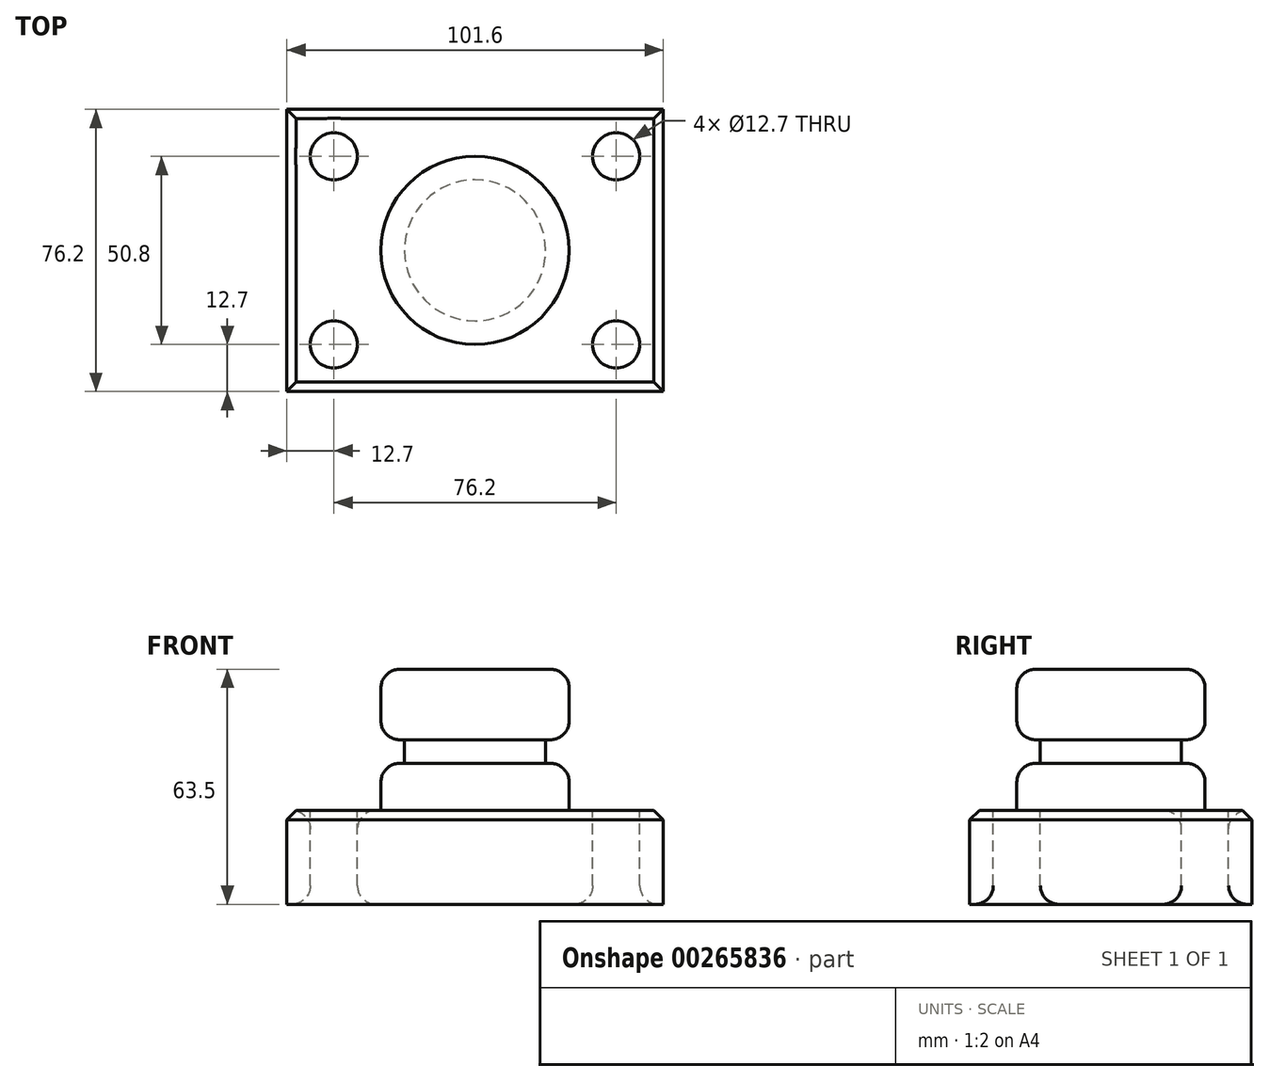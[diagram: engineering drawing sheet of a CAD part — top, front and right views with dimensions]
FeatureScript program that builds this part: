
annotation { "Feature Type Name" : "Feature", "Feature Type Description" : "" }
export const myFeature = defineFeature(function(context is Context, id is Id, definition is map)
    precondition{}
    {
        {
            var Q0;
            Q0=qCreatedBy(makeId("Top.planeOp"),FACE);
            var sketch = newSketch(context, id + "F0", { "sketchPlane" : qUnion([Q0])});
            skLineSegment(sketch, "E0.bottom", {"start": v(-50.8, 38.1) * mm, "end": v(50.8, 38.1) * mm});
            skLineSegment(sketch, "E0.top", {"start": v(-50.8, -38.1) * mm, "end": v(50.8, -38.1) * mm});
            skLineSegment(sketch, "E0.left", {"start": v(-50.8, 38.1) * mm, "end": v(-50.8, -38.1) * mm});
            skLineSegment(sketch, "E0.right", {"start": v(50.8, 38.1) * mm, "end": v(50.8, -38.1) * mm});
            skPoint(sketch, "E0.middle", {"position": v(0, 0) * mm});
            skSolve(sketch);
        }
        {
            var Q0;
            Q0 = qSketchRegion(id + "F0", true);
            extrude(context, id + "F1", {"entities" : qUnion([Q0]), "depth" : 25.4 * mm});
        }
        {
            var Q0;
            Q0=qCreatedBy(makeId("Top.planeOp"),FACE);
            var sketch = newSketch(context, id + "F2", { "sketchPlane" : qUnion([Q0])});
            skCircle(sketch, "E1", {"center": v(-38.1, 25.4) * mm, "radius": 6.35 * mm});
            skCircle(sketch, "E2", {"center": v(38.1, 25.4) * mm, "radius": 6.35 * mm});
            skCircle(sketch, "E3", {"center": v(-38.1, -25.4) * mm, "radius": 6.35 * mm});
            skCircle(sketch, "E4", {"center": v(38.1, -25.4) * mm, "radius": 6.35 * mm});
            skSolve(sketch);
        }
        {
            var Q0;
            Q0 = qSketchRegion(id + "F2", true);
            extrude(context, id + "F3", {"entities" : qUnion([Q0]), "operationType" : NewBodyOperationType.REMOVE, "oppositeDirection" : true, "depth" : 25.4 * mm, "hasSecondDirection" : true, "secondDirectionOppositeDirection" : false, "secondDirectionDepth" : 25.4 * mm});
        }
        {
            var Q0;
            Q0=qCreatedBy(makeId("Front.planeOp"),FACE);
            var sketch = newSketch(context, id + "F4", { "sketchPlane" : qUnion([Q0])});
            skLineSegment(sketch, "E5.bottom", {"start": v(0, 63.5) * mm, "end": v(25.4, 63.5) * mm});
            skLineSegment(sketch, "E5.top", {"start": v(0, 25.4) * mm, "end": v(25.4, 25.4) * mm});
            skLineSegment(sketch, "E5.left", {"start": v(0, 63.5) * mm, "end": v(0, 25.4) * mm});
            skLineSegment(sketch, "E5.right", {"start": v(25.4, 63.5) * mm, "end": v(25.4, 25.4) * mm});
            skSolve(sketch);
        }
        {
            var Q0;
            Q0 = qSketchRegion(id + "F4", true);
            var Q1;
            Q1=sQuery(id+"F4.wireOp",EDGE,"E5.left");
            revolve(context, id + "F5", {"operationType" : NewBodyOperationType.ADD, "entities" : qUnion([Q0]), "axis" : qUnion([Q1]), "revolveType" : RevolveType.FULL});
        }
        {
            var Q0;
            Q0=qCreatedBy(makeId("Right.planeOp"),FACE);
            var sketch = newSketch(context, id + "F6", { "sketchPlane" : qUnion([Q0])});
            skLineSegment(sketch, "E6.bottom", {"start": v(-38.1, 44.45) * mm, "end": v(-19.05, 44.45) * mm});
            skLineSegment(sketch, "E6.top", {"start": v(-38.1, 38.1) * mm, "end": v(-19.05, 38.1) * mm});
            skLineSegment(sketch, "E6.left", {"start": v(-38.1, 44.45) * mm, "end": v(-38.1, 38.1) * mm});
            skLineSegment(sketch, "E6.right", {"start": v(-19.05, 44.45) * mm, "end": v(-19.05, 38.1) * mm});
            skSolve(sketch);
        }
        {
            var Q0;
            Q0 = qSketchRegion(id + "F6", true);
            var Q1;
            Q1=makeQuery(id+"F5.opRevolve","SWEPT_FACE",FACE,{"disambiguationData":[OSD([sQuery(id+"F4.wireOp",EDGE,"E5.right")])]});
            revolve(context, id + "F7", {"operationType" : NewBodyOperationType.REMOVE, "entities" : qUnion([Q0]), "axis" : qUnion([Q1]), "revolveType" : RevolveType.FULL, "oppositeDirection" : true});
        }
        {
            var Q0;
            Q0=makeQuery(id+"F1.opExtrude","CAP_EDGE",EDGE,{"disambiguationData":[OSD([sQuery(id+"F0.wireOp",EDGE,"E0.top")])],"isStart":false});
            var Q1;
            Q1=makeQuery(id+"F1.opExtrude","CAP_EDGE",EDGE,{"disambiguationData":[OSD([sQuery(id+"F0.wireOp",EDGE,"E0.left")])],"isStart":false});
            var Q2;
            Q2=makeQuery(id+"F1.opExtrude","CAP_EDGE",EDGE,{"disambiguationData":[OSD([sQuery(id+"F0.wireOp",EDGE,"E0.bottom")])],"isStart":false});
            var Q3;
            Q3=makeQuery(id+"F1.opExtrude","CAP_EDGE",EDGE,{"disambiguationData":[OSD([sQuery(id+"F0.wireOp",EDGE,"E0.right")])],"isStart":false});
            chamfer(context, id + "F8", {"entities" : qUnion([Q0, Q1, Q2, Q3]), "width" : 2.54 * mm, "tangentPropagation" : true});
        }
        {
            var Q0;
            Q0=makeQuery(id+"F5.opRevolve","SWEPT_EDGE",EDGE,{"disambiguationData":[OSD([sQuery(id+"F4.wireOp",EDGE,"E5.top"),sQuery(id+"F4.wireOp",EDGE,"E5.right")])]});
            var Q1;
            Q1=makeQuery(id+"F7.boolean.opBoolean","INTERSECT",EDGE,{"derivedFrom":[makeQuery(id+"F5.opRevolve","SWEPT_FACE",FACE,{"disambiguationData":[OSD([sQuery(id+"F4.wireOp",EDGE,"E5.right")])]}),makeQuery(id+"F7.opRevolve","SWEPT_FACE",FACE,{"disambiguationData":[OSD([sQuery(id+"F6.wireOp",EDGE,"E6.bottom")])]})]});
            var Q2;
            Q2=makeQuery(id+"F7.boolean.opBoolean","INTERSECT",EDGE,{"derivedFrom":[makeQuery(id+"F5.opRevolve","SWEPT_FACE",FACE,{"disambiguationData":[OSD([sQuery(id+"F4.wireOp",EDGE,"E5.right")])]}),makeQuery(id+"F7.opRevolve","SWEPT_FACE",FACE,{"disambiguationData":[OSD([sQuery(id+"F6.wireOp",EDGE,"E6.top")])]})]});
            var Q3;
            Q3=makeQuery(id+"F5.opRevolve","SWEPT_EDGE",EDGE,{"disambiguationData":[OSD([sQuery(id+"F4.wireOp",EDGE,"E5.bottom"),sQuery(id+"F4.wireOp",EDGE,"E5.right")])]});
            fillet(context, id + "F9", {"entities" : qUnion([Q0, Q1, Q2, Q3]), "radius" : 5.08 * mm, "tangentPropagation" : true, "allowEdgeOverflow" : false});
        }
        {
            var Q0;
            Q0=makeQuery(id+"F3.boolean.opBoolean","COPY",EDGE,{"derivedFrom":makeQuery(id+"F3.opExtrude","CAP_EDGE",EDGE,{"disambiguationData":[OSD([sQuery(id+"F2.wireOp",EDGE,"E2")])],"isStart":true})});
            var Q1;
            Q1=makeQuery(id+"F3.boolean.opBoolean","COPY",EDGE,{"derivedFrom":makeQuery(id+"F3.opExtrude","CAP_EDGE",EDGE,{"disambiguationData":[OSD([sQuery(id+"F2.wireOp",EDGE,"E4")])],"isStart":true})});
            var Q2;
            Q2=makeQuery(id+"F3.boolean.opBoolean","COPY",EDGE,{"derivedFrom":makeQuery(id+"F3.opExtrude","CAP_EDGE",EDGE,{"disambiguationData":[OSD([sQuery(id+"F2.wireOp",EDGE,"E3")])],"isStart":true})});
            var Q3;
            Q3=makeQuery(id+"F3.boolean.opBoolean","COPY",EDGE,{"derivedFrom":makeQuery(id+"F3.opExtrude","CAP_EDGE",EDGE,{"disambiguationData":[OSD([sQuery(id+"F2.wireOp",EDGE,"E1")])],"isStart":true})});
            var Q4;
            Q4=makeQuery(id+"F3.boolean.opBoolean","INTERSECT",EDGE,{"derivedFrom":[makeQuery(id+"F1.opExtrude","CAP_FACE",FACE,{"disambiguationData":[OSD([sQuery(id+"F0.wireOp",EDGE,"E0.bottom"),sQuery(id+"F0.wireOp",EDGE,"E0.top"),sQuery(id+"F0.wireOp",EDGE,"E0.left"),sQuery(id+"F0.wireOp",EDGE,"E0.right")])],"isStart":true}),makeQuery(id+"F3.opExtrude","SWEPT_FACE",FACE,{"disambiguationData":[OSD([sQuery(id+"F2.wireOp",EDGE,"E2")])]})]});
            var Q5;
            Q5=makeQuery(id+"F3.boolean.opBoolean","INTERSECT",EDGE,{"derivedFrom":[makeQuery(id+"F1.opExtrude","CAP_FACE",FACE,{"disambiguationData":[OSD([sQuery(id+"F0.wireOp",EDGE,"E0.bottom"),sQuery(id+"F0.wireOp",EDGE,"E0.top"),sQuery(id+"F0.wireOp",EDGE,"E0.left"),sQuery(id+"F0.wireOp",EDGE,"E0.right")])],"isStart":true}),makeQuery(id+"F3.opExtrude","SWEPT_FACE",FACE,{"disambiguationData":[OSD([sQuery(id+"F2.wireOp",EDGE,"E4")])]})]});
            var Q6;
            Q6=makeQuery(id+"F3.boolean.opBoolean","INTERSECT",EDGE,{"derivedFrom":[makeQuery(id+"F1.opExtrude","CAP_FACE",FACE,{"disambiguationData":[OSD([sQuery(id+"F0.wireOp",EDGE,"E0.bottom"),sQuery(id+"F0.wireOp",EDGE,"E0.top"),sQuery(id+"F0.wireOp",EDGE,"E0.left"),sQuery(id+"F0.wireOp",EDGE,"E0.right")])],"isStart":true}),makeQuery(id+"F3.opExtrude","SWEPT_FACE",FACE,{"disambiguationData":[OSD([sQuery(id+"F2.wireOp",EDGE,"E3")])]})]});
            var Q7;
            Q7=makeQuery(id+"F3.boolean.opBoolean","COPY",FACE,{"derivedFrom":makeQuery(id+"F3.opExtrude","SWEPT_FACE",FACE,{"disambiguationData":[OSD([sQuery(id+"F2.wireOp",EDGE,"E1")])]})});
            fillet(context, id + "F10", {"entities" : qUnion([Q0, Q1, Q2, Q3, Q4, Q5, Q6, Q7]), "radius" : 5.08 * mm, "tangentPropagation" : true, "allowEdgeOverflow" : false});
        }
    });
